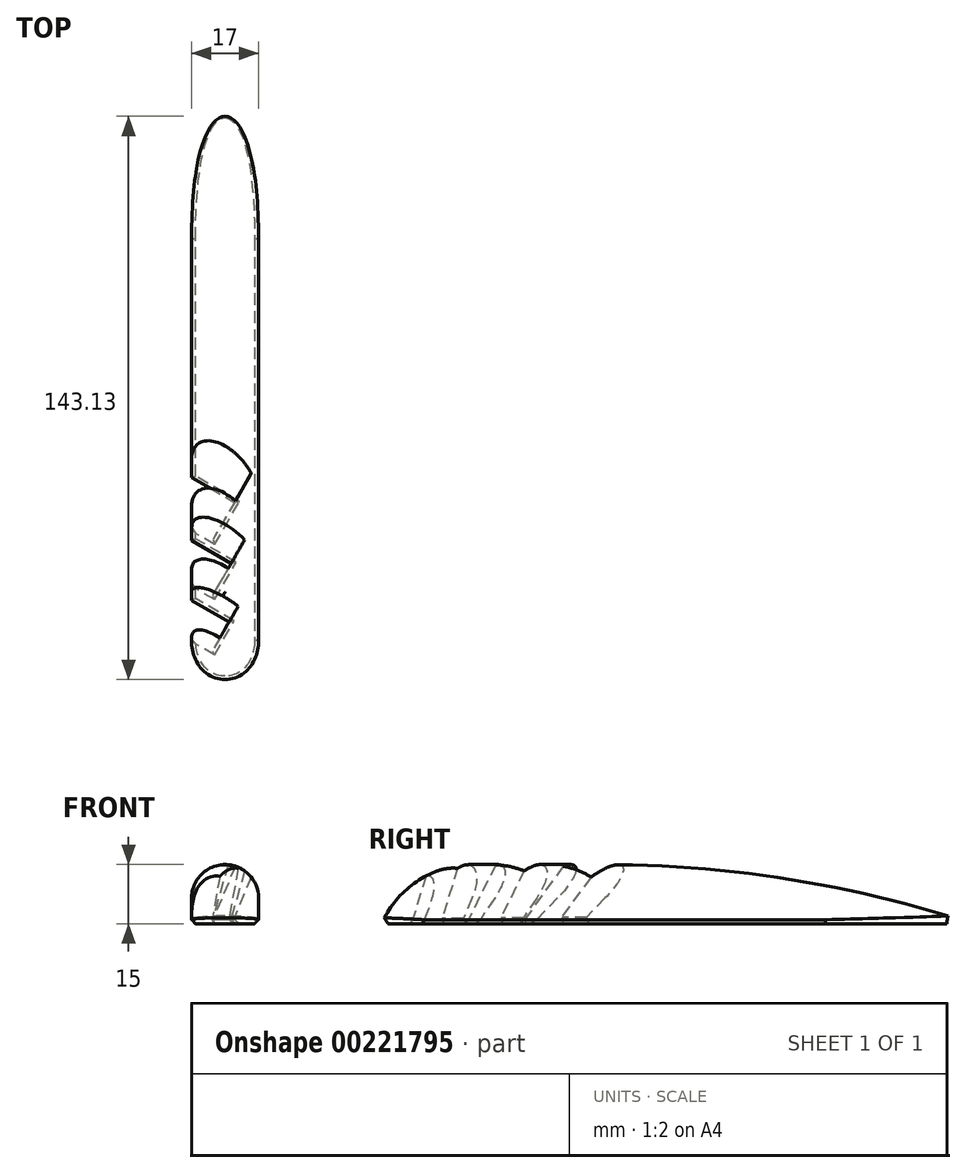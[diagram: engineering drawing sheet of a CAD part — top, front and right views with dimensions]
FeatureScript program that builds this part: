
annotation { "Feature Type Name" : "Feature", "Feature Type Description" : "" }
export const myFeature = defineFeature(function(context is Context, id is Id, definition is map)
    precondition{}
    {
        {
            var Q0;
            Q0=qCreatedBy(makeId("Top.planeOp"),FACE);
            var sketch = newSketch(context, id + "F0", { "sketchPlane" : qUnion([Q0])});
            skLineSegment(sketch, "E0.bottom", {"start": v(8.5, 75) * mm, "end": v(-8.5, 75) * mm});
            skLineSegment(sketch, "E0.top", {"start": v(8.5, -75) * mm, "end": v(-8.5, -75) * mm});
            skLineSegment(sketch, "E0.left", {"start": v(8.5, 75) * mm, "end": v(8.5, -75) * mm});
            skLineSegment(sketch, "E0.right", {"start": v(-8.5, 75) * mm, "end": v(-8.5, -75) * mm});
            skPoint(sketch, "E0.middle", {"position": v(0, 0) * mm});
            skSolve(sketch);
        }
        {
            var Q0;
            Q0=makeQuery(id+"F0.imprint","IMPRINT",FACE,{"disambiguationData":[TD([[makeQuery(id+"F0.imprint","IMPRINT",EDGE,{"derivedFrom":sQuery(id+"F0.wireOp",EDGE,"E0.bottom")}),1.0]])]});
            extrude(context, id + "F1", {"entities" : qUnion([Q0]), "depth" : 15 * mm, "offsetDistance" : 25 * mm});
        }
        {
            var Q0;
            Q0=makeQuery(id+"F1.opExtrude","CAP_FACE",FACE,{"disambiguationData":[OSD([sQuery(id+"F0.wireOp",EDGE,"E0.bottom"),sQuery(id+"F0.wireOp",EDGE,"E0.top"),sQuery(id+"F0.wireOp",EDGE,"E0.left"),sQuery(id+"F0.wireOp",EDGE,"E0.right")])],"isStart":true});
            var sketch = newSketch(context, id + "F2", { "sketchPlane" : qUnion([Q0])});
            skLineSegment(sketch, "E1", {"start": v(-3.5, 75) * mm, "end": v(-3.5, -75) * mm, "construction": true});
            skLineSegment(sketch, "E2", {"start": v(-3.5, 67.5) * mm, "end": v(-8.5, 64.61) * mm});
            skLineSegment(sketch, "E3.0.1.0", {"start": v(-3.5, 53.5) * mm, "end": v(-8.5, 50.61) * mm});
            skLineSegment(sketch, "E3.0.2.0", {"start": v(-3.5, 39.5) * mm, "end": v(-8.5, 36.61) * mm});
            skLineSegment(sketch, "E3.direction1", {"start": v(-8.5, 64.61) * mm, "end": v(-8.5, 64.61) * mm});
            skLineSegment(sketch, "E3.direction2", {"start": v(-8.5, 64.61) * mm, "end": v(-8.5, 50.61) * mm, "construction": true});
            skSolve(sketch);
        }
        {
            var Q0;
            Q0=sQuery(id+"F2.wireOp",EDGE,"E2");
            var Q1;
            {var subQ1=makeQuery(id+"F1.opExtrude","CAP_EDGE",EDGE,{"disambiguationData":[OSD([sQuery(id+"F0.wireOp",EDGE,"E0.bottom")])],"isStart":true});Q1=makeQuery(id+"F2.imprint","IMPRINT",FACE,{"disambiguationData":[TD([[makeQuery(id+"F2.imprint","IMPRINT",EDGE,{"derivedFrom":subQ1}),-1.0]])]});}
            cPlane(context, id + "F3", {"entities" : qUnion([Q0, Q1]), "cplaneType" : CPlaneType.LINE_ANGLE, "offset" : 25 * mm, "angle" : 20 * degree, "width" : 150 * mm, "height" : 150 * mm});
        }
        {
            var Q0;
            Q0=qCreatedBy(id+"F3.planeOp",FACE);
            var sketch = newSketch(context, id + "F4", { "sketchPlane" : qUnion([Q0])});
            skLineSegment(sketch, "E4.0", {"start": v(0.02, -64.38) * mm, "end": v(-5.05, -61.62) * mm});
            skLineSegment(sketch, "E4.1", {"start": v(-14.68, 67.02) * mm, "end": v(-6.97, -76.04) * mm});
            skLineSegment(sketch, "E5", {"start": v(-5.05, -61.62) * mm, "end": v(-7.82, -60.12) * mm});
            skLineSegment(sketch, "E6", {"start": v(0.02, -64.38) * mm, "end": v(3.84, -57.35) * mm});
            skLineSegment(sketch, "E7", {"start": v(3.84, -57.35) * mm, "end": v(-8.33, -50.75) * mm});
            skSolve(sketch);
        }
        {
            var Q0;
            Q0=makeQuery(id+"F4.imprint","IMPRINT",FACE,{"disambiguationData":[TD([[makeQuery(id+"F4.imprint","IMPRINT",EDGE,{"derivedFrom":sQuery(id+"F4.wireOp",EDGE,"E4.0")}),-1.0]])]});
            var Q1;
            Q1=makeQuery(id+"F1.opExtrude","CAP_FACE",FACE,{"disambiguationData":[OSD([sQuery(id+"F0.wireOp",EDGE,"E0.bottom"),sQuery(id+"F0.wireOp",EDGE,"E0.top"),sQuery(id+"F0.wireOp",EDGE,"E0.left"),sQuery(id+"F0.wireOp",EDGE,"E0.right")])],"isStart":false});
            extrude(context, id + "F5", {"entities" : qUnion([Q0]), "operationType" : NewBodyOperationType.REMOVE, "endBound" : BoundingType.UP_TO_SURFACE, "depth" : 25 * mm, "endBoundEntityFace" : qUnion([Q1]), "offsetDistance" : 25 * mm});
        }
        {
            var Q0;
            Q0=sQuery(id+"F2.wireOp",EDGE,"E3.0.1.0");
            var Q1;
            {var subQ1=makeQuery(id+"F1.opExtrude","CAP_EDGE",EDGE,{"disambiguationData":[OSD([sQuery(id+"F0.wireOp",EDGE,"E0.bottom")])],"isStart":true});Q1=makeQuery(id+"F2.imprint","IMPRINT",FACE,{"disambiguationData":[TD([[makeQuery(id+"F2.imprint","IMPRINT",EDGE,{"derivedFrom":subQ1}),-1.0]])]});}
            cPlane(context, id + "F6", {"entities" : qUnion([Q0, Q1]), "cplaneType" : CPlaneType.LINE_ANGLE, "offset" : 25 * mm, "angle" : 30 * degree, "width" : 150 * mm, "height" : 150 * mm});
        }
        {
            var Q0;
            Q0=qCreatedBy(id+"F6.planeOp",FACE);
            var sketch = newSketch(context, id + "F7", { "sketchPlane" : qUnion([Q0])});
            skLineSegment(sketch, "E8.0", {"start": v(2.6, -47.85) * mm, "end": v(-2.57, -45.27) * mm});
            skLineSegment(sketch, "E8.1", {"start": v(-19.97, 60.37) * mm, "end": v(-6.16, -50.07) * mm});
            skLineSegment(sketch, "E9", {"start": v(-2.57, -45.27) * mm, "end": v(-7.04, -43.03) * mm});
            skLineSegment(sketch, "E10", {"start": v(2.6, -47.85) * mm, "end": v(6.17, -40.7) * mm});
            skLineSegment(sketch, "E11", {"start": v(6.17, -40.7) * mm, "end": v(-8.24, -33.5) * mm});
            skSolve(sketch);
        }
        {
            var Q0;
            Q0=makeQuery(id+"F7.imprint","IMPRINT",FACE,{"disambiguationData":[TD([[makeQuery(id+"F7.imprint","IMPRINT",EDGE,{"derivedFrom":sQuery(id+"F7.wireOp",EDGE,"E8.0")}),-1.0]])]});
            var Q1;
            Q1=makeQuery(id+"F1.opExtrude","CAP_FACE",FACE,{"disambiguationData":[OSD([sQuery(id+"F0.wireOp",EDGE,"E0.bottom"),sQuery(id+"F0.wireOp",EDGE,"E0.top"),sQuery(id+"F0.wireOp",EDGE,"E0.left"),sQuery(id+"F0.wireOp",EDGE,"E0.right")])],"isStart":false});
            extrude(context, id + "F8", {"entities" : qUnion([Q0]), "operationType" : NewBodyOperationType.REMOVE, "endBound" : BoundingType.UP_TO_SURFACE, "depth" : 25 * mm, "endBoundEntityFace" : qUnion([Q1]), "offsetDistance" : 25 * mm});
        }
        {
            var Q0;
            Q0=sQuery(id+"F2.wireOp",EDGE,"E3.0.2.0");
            var Q1;
            {var subQ1=makeQuery(id+"F1.opExtrude","CAP_EDGE",EDGE,{"disambiguationData":[OSD([sQuery(id+"F0.wireOp",EDGE,"E0.bottom")])],"isStart":true});Q1=makeQuery(id+"F2.imprint","IMPRINT",FACE,{"disambiguationData":[TD([[makeQuery(id+"F2.imprint","IMPRINT",EDGE,{"derivedFrom":subQ1}),-1.0]])]});}
            cPlane(context, id + "F9", {"entities" : qUnion([Q0, Q1]), "cplaneType" : CPlaneType.LINE_ANGLE, "offset" : 25 * mm, "angle" : 40 * degree, "width" : 150 * mm, "height" : 150 * mm});
        }
        {
            var Q0;
            Q0=qCreatedBy(id+"F9.planeOp",FACE);
            var sketch = newSketch(context, id + "F10", { "sketchPlane" : qUnion([Q0])});
            skLineSegment(sketch, "E12.0", {"start": v(4.15, -31.95) * mm, "end": v(-1.13, -29.62) * mm});
            skLineSegment(sketch, "E12.1", {"start": v(-26.12, 51.85) * mm, "end": v(-6.3, -33.04) * mm});
            skLineSegment(sketch, "E13", {"start": v(-1.13, -29.62) * mm, "end": v(-7.78, -26.68) * mm});
            skLineSegment(sketch, "E14", {"start": v(4.15, -31.95) * mm, "end": v(7.38, -24.64) * mm});
            skLineSegment(sketch, "E15", {"start": v(7.38, -24.64) * mm, "end": v(-10.06, -16.92) * mm});
            skSolve(sketch);
        }
        {
            var Q0;
            Q0=makeQuery(id+"F10.imprint","IMPRINT",FACE,{"disambiguationData":[TD([[makeQuery(id+"F10.imprint","IMPRINT",EDGE,{"derivedFrom":sQuery(id+"F10.wireOp",EDGE,"E12.0")}),-1.0]])]});
            var Q1;
            {var subQ0=sQuery(id+"F0.wireOp",EDGE,"E0.bottom");var subQ1=sQuery(id+"F0.wireOp",EDGE,"E0.right");var subQ2=sQuery(id+"F0.wireOp",EDGE,"E0.left");Q1=makeQuery(id+"F8.boolean.opBoolean","SPLIT",FACE,{"disambiguationData":[TD([makeQuery(id+"F1.opExtrude","SWEPT_FACE",FACE,{"disambiguationData":[OSD([subQ0])]})])],"derivedFrom":makeQuery(id+"F1.opExtrude","CAP_FACE",FACE,{"disambiguationData":[OSD([subQ0,sQuery(id+"F0.wireOp",EDGE,"E0.top"),subQ2,subQ1])],"isStart":false})});}
            extrude(context, id + "F11", {"entities" : qUnion([Q0]), "operationType" : NewBodyOperationType.REMOVE, "endBound" : BoundingType.UP_TO_SURFACE, "depth" : 25 * mm, "endBoundEntityFace" : qUnion([Q1]), "offsetDistance" : 25 * mm});
        }
        {
            var Q0;
            Q0=makeQuery(id+"F1.opExtrude","CAP_EDGE",EDGE,{"disambiguationData":[OSD([sQuery(id+"F0.wireOp",EDGE,"E0.bottom")])],"isStart":false});
            fillet(context, id + "F12", {"entities" : qUnion([Q0]), "radius" : 300 * mm, "tangentPropagation" : true, "allowEdgeOverflow" : false});
        }
        {
            var Q0;
            Q0=makeQuery(id+"F1.opExtrude","CAP_EDGE",EDGE,{"disambiguationData":[OSD([sQuery(id+"F0.wireOp",EDGE,"E0.top")])],"isStart":false});
            fillet(context, id + "F13", {"entities" : qUnion([Q0]), "radius" : 25 * mm, "tangentPropagation" : true, "allowEdgeOverflow" : false});
        }
        {
            var Q0;
            {var subQ0=sQuery(id+"F0.wireOp",EDGE,"E0.bottom");var subQ1=makeQuery(id+"F1.opExtrude","SWEPT_FACE",FACE,{"disambiguationData":[OSD([subQ0])]});var subQ2=sQuery(id+"F0.wireOp",EDGE,"E0.right");Q0=makeQuery(id+"F12.opFillet","BLEND_EDGE",EDGE,{"blendedFrom":[makeQuery(id+"F1.opExtrude","CAP_EDGE",EDGE,{"disambiguationData":[OSD([subQ0])],"isStart":false}),makeQuery(id+"F11.boolean.opBoolean","SPLIT",FACE,{"disambiguationData":[TD([subQ1])],"derivedFrom":makeQuery(id+"F8.boolean.opBoolean","SPLIT",FACE,{"disambiguationData":[TD([subQ1])],"derivedFrom":makeQuery(id+"F5.boolean.opBoolean","SPLIT",FACE,{"disambiguationData":[TD([subQ1])],"derivedFrom":makeQuery(id+"F1.opExtrude","SWEPT_FACE",FACE,{"disambiguationData":[OSD([subQ2])]})})})})],"blendedInto":[makeQuery(id+"F11.boolean.opBoolean","SPLIT",FACE,{"disambiguationData":[TD([subQ1])],"derivedFrom":makeQuery(id+"F8.boolean.opBoolean","SPLIT",FACE,{"disambiguationData":[TD([subQ1])],"derivedFrom":makeQuery(id+"F5.boolean.opBoolean","SPLIT",FACE,{"disambiguationData":[TD([subQ1])],"derivedFrom":makeQuery(id+"F1.opExtrude","SWEPT_FACE",FACE,{"disambiguationData":[OSD([subQ2])]})})})})]});}
            var Q1;
            {var subQ0=sQuery(id+"F0.wireOp",EDGE,"E0.right");var subQ1=sQuery(id+"F0.wireOp",EDGE,"E0.bottom");var subQ4=makeQuery(id+"F8.opExtrude","SWEPT_FACE",FACE,{"disambiguationData":[OSD([sQuery(id+"F7.wireOp",EDGE,"E11")])]});var subQ5=makeQuery(id+"F1.opExtrude","SWEPT_FACE",FACE,{"disambiguationData":[OSD([subQ1])]});Q1=makeQuery(id+"F11.boolean.opBoolean","SPLIT",EDGE,{"disambiguationData":[TD([makeQuery(id+"F8.boolean.opBoolean","COPY",FACE,{"derivedFrom":subQ4})])],"derivedFrom":makeQuery(id+"F8.boolean.opBoolean","SPLIT",EDGE,{"disambiguationData":[TD([subQ5])],"derivedFrom":makeQuery(id+"F5.boolean.opBoolean","SPLIT",EDGE,{"disambiguationData":[TD([subQ5])],"derivedFrom":makeQuery(id+"F1.opExtrude","CAP_EDGE",EDGE,{"disambiguationData":[OSD([subQ0])],"isStart":false})})})});}
            var Q2;
            {var subQ0=sQuery(id+"F0.wireOp",EDGE,"E0.right");var subQ1=sQuery(id+"F0.wireOp",EDGE,"E0.bottom");var subQ4=makeQuery(id+"F5.opExtrude","SWEPT_FACE",FACE,{"disambiguationData":[OSD([sQuery(id+"F4.wireOp",EDGE,"E7")])]});Q2=makeQuery(id+"F8.boolean.opBoolean","SPLIT",EDGE,{"disambiguationData":[TD([makeQuery(id+"F5.boolean.opBoolean","COPY",FACE,{"derivedFrom":subQ4})])],"derivedFrom":makeQuery(id+"F5.boolean.opBoolean","SPLIT",EDGE,{"disambiguationData":[TD([makeQuery(id+"F1.opExtrude","SWEPT_FACE",FACE,{"disambiguationData":[OSD([subQ1])]})])],"derivedFrom":makeQuery(id+"F1.opExtrude","CAP_EDGE",EDGE,{"disambiguationData":[OSD([subQ0])],"isStart":false})})});}
            var Q3;
            {var subQ0=sQuery(id+"F0.wireOp",EDGE,"E0.right");var subQ2=sQuery(id+"F0.wireOp",EDGE,"E0.top");Q3=makeQuery(id+"F13.opFillet","BLEND_EDGE",EDGE,{"blendedFrom":[makeQuery(id+"F1.opExtrude","CAP_EDGE",EDGE,{"disambiguationData":[OSD([subQ2])],"isStart":false}),makeQuery(id+"F5.boolean.opBoolean","SPLIT",FACE,{"disambiguationData":[TD([makeQuery(id+"F1.opExtrude","SWEPT_FACE",FACE,{"disambiguationData":[OSD([subQ2])]})])],"derivedFrom":makeQuery(id+"F1.opExtrude","SWEPT_FACE",FACE,{"disambiguationData":[OSD([subQ0])]})})],"blendedInto":[makeQuery(id+"F5.boolean.opBoolean","SPLIT",FACE,{"disambiguationData":[TD([makeQuery(id+"F1.opExtrude","SWEPT_FACE",FACE,{"disambiguationData":[OSD([subQ2])]})])],"derivedFrom":makeQuery(id+"F1.opExtrude","SWEPT_FACE",FACE,{"disambiguationData":[OSD([subQ0])]})})]});}
            var Q4;
            Q4=makeQuery(id+"F12.opFillet","BLEND_EDGE",EDGE,{"blendedFrom":[makeQuery(id+"F1.opExtrude","CAP_EDGE",EDGE,{"disambiguationData":[OSD([sQuery(id+"F0.wireOp",EDGE,"E0.bottom")])],"isStart":false}),makeQuery(id+"F1.opExtrude","SWEPT_FACE",FACE,{"disambiguationData":[OSD([sQuery(id+"F0.wireOp",EDGE,"E0.left")])]})],"blendedInto":[makeQuery(id+"F1.opExtrude","SWEPT_FACE",FACE,{"disambiguationData":[OSD([sQuery(id+"F0.wireOp",EDGE,"E0.left")])]})]});
            fillet(context, id + "F14", {"entities" : qUnion([Q0, Q1, Q2, Q3, Q4]), "radius" : 8.5 * mm, "tangentPropagation" : true, "allowEdgeOverflow" : false});
        }
        {
            var Q0;
            Q0=makeQuery(id+"F1.opExtrude","CAP_EDGE",EDGE,{"disambiguationData":[OSD([sQuery(id+"F0.wireOp",EDGE,"E0.left")])],"isStart":true});
            var Q1;
            {var subQ0=sQuery(id+"F0.wireOp",EDGE,"E0.right");var subQ1=sQuery(id+"F0.wireOp",EDGE,"E0.bottom");var subQ4=makeQuery(id+"F8.opExtrude","SWEPT_FACE",FACE,{"disambiguationData":[OSD([sQuery(id+"F7.wireOp",EDGE,"E11")])]});var subQ5=makeQuery(id+"F1.opExtrude","SWEPT_FACE",FACE,{"disambiguationData":[OSD([subQ1])]});Q1=makeQuery(id+"F11.boolean.opBoolean","SPLIT",EDGE,{"disambiguationData":[TD([makeQuery(id+"F8.boolean.opBoolean","COPY",FACE,{"derivedFrom":subQ4})])],"derivedFrom":makeQuery(id+"F8.boolean.opBoolean","SPLIT",EDGE,{"disambiguationData":[TD([subQ5])],"derivedFrom":makeQuery(id+"F5.boolean.opBoolean","SPLIT",EDGE,{"disambiguationData":[TD([subQ5])],"derivedFrom":makeQuery(id+"F1.opExtrude","CAP_EDGE",EDGE,{"disambiguationData":[OSD([subQ0])],"isStart":true})})})});}
            var Q2;
            {var subQ0=sQuery(id+"F0.wireOp",EDGE,"E0.right");var subQ1=sQuery(id+"F0.wireOp",EDGE,"E0.bottom");var subQ4=makeQuery(id+"F5.opExtrude","SWEPT_FACE",FACE,{"disambiguationData":[OSD([sQuery(id+"F4.wireOp",EDGE,"E7")])]});Q2=makeQuery(id+"F8.boolean.opBoolean","SPLIT",EDGE,{"disambiguationData":[TD([makeQuery(id+"F5.boolean.opBoolean","COPY",FACE,{"derivedFrom":subQ4})])],"derivedFrom":makeQuery(id+"F5.boolean.opBoolean","SPLIT",EDGE,{"disambiguationData":[TD([makeQuery(id+"F1.opExtrude","SWEPT_FACE",FACE,{"disambiguationData":[OSD([subQ1])]})])],"derivedFrom":makeQuery(id+"F1.opExtrude","CAP_EDGE",EDGE,{"disambiguationData":[OSD([subQ0])],"isStart":true})})});}
            chamfer(context, id + "F15", {"entities" : qUnion([Q0, Q1, Q2]), "width" : 1 * mm, "tangentPropagation" : true});
        }
        {
            var Q0;
            Q0=makeQuery(id+"F11.boolean.opBoolean","INTERSECT",EDGE,{"derivedFrom":[makeQuery(id+"F1.opExtrude","CAP_FACE",FACE,{"disambiguationData":[OSD([sQuery(id+"F0.wireOp",EDGE,"E0.bottom"),sQuery(id+"F0.wireOp",EDGE,"E0.top"),sQuery(id+"F0.wireOp",EDGE,"E0.left"),sQuery(id+"F0.wireOp",EDGE,"E0.right")])],"isStart":true}),makeQuery(id+"F11.opExtrude","SWEPT_FACE",FACE,{"disambiguationData":[OSD([sQuery(id+"F10.wireOp",EDGE,"E15")])]})]});
            var Q1;
            Q1=makeQuery(id+"F11.boolean.opBoolean","INTERSECT",EDGE,{"derivedFrom":[makeQuery(id+"F1.opExtrude","CAP_FACE",FACE,{"disambiguationData":[OSD([sQuery(id+"F0.wireOp",EDGE,"E0.bottom"),sQuery(id+"F0.wireOp",EDGE,"E0.top"),sQuery(id+"F0.wireOp",EDGE,"E0.left"),sQuery(id+"F0.wireOp",EDGE,"E0.right")])],"isStart":true}),makeQuery(id+"F11.opExtrude","SWEPT_FACE",FACE,{"disambiguationData":[OSD([sQuery(id+"F10.wireOp",EDGE,"E14")])]})]});
            var Q2;
            Q2=makeQuery(id+"F11.boolean.opBoolean","COPY",EDGE,{"derivedFrom":makeQuery(id+"F11.opExtrude","CAP_EDGE",EDGE,{"disambiguationData":[OSD([sQuery(id+"F10.wireOp",EDGE,"E12.0"),sQuery(id+"F10.wireOp",EDGE,"E13")])],"isStart":true})});
            var Q3;
            Q3=makeQuery(id+"F8.boolean.opBoolean","INTERSECT",EDGE,{"derivedFrom":[makeQuery(id+"F1.opExtrude","CAP_FACE",FACE,{"disambiguationData":[OSD([sQuery(id+"F0.wireOp",EDGE,"E0.bottom"),sQuery(id+"F0.wireOp",EDGE,"E0.top"),sQuery(id+"F0.wireOp",EDGE,"E0.left"),sQuery(id+"F0.wireOp",EDGE,"E0.right")])],"isStart":true}),makeQuery(id+"F8.opExtrude","SWEPT_FACE",FACE,{"disambiguationData":[OSD([sQuery(id+"F7.wireOp",EDGE,"E11")])]})]});
            var Q4;
            Q4=makeQuery(id+"F8.boolean.opBoolean","INTERSECT",EDGE,{"derivedFrom":[makeQuery(id+"F1.opExtrude","CAP_FACE",FACE,{"disambiguationData":[OSD([sQuery(id+"F0.wireOp",EDGE,"E0.bottom"),sQuery(id+"F0.wireOp",EDGE,"E0.top"),sQuery(id+"F0.wireOp",EDGE,"E0.left"),sQuery(id+"F0.wireOp",EDGE,"E0.right")])],"isStart":true}),makeQuery(id+"F8.opExtrude","SWEPT_FACE",FACE,{"disambiguationData":[OSD([sQuery(id+"F7.wireOp",EDGE,"E10")])]})]});
            var Q5;
            Q5=makeQuery(id+"F8.boolean.opBoolean","COPY",EDGE,{"derivedFrom":makeQuery(id+"F8.opExtrude","CAP_EDGE",EDGE,{"disambiguationData":[OSD([sQuery(id+"F7.wireOp",EDGE,"E8.0"),sQuery(id+"F7.wireOp",EDGE,"E9")])],"isStart":true})});
            var Q6;
            Q6=makeQuery(id+"F5.boolean.opBoolean","INTERSECT",EDGE,{"derivedFrom":[makeQuery(id+"F1.opExtrude","CAP_FACE",FACE,{"disambiguationData":[OSD([sQuery(id+"F0.wireOp",EDGE,"E0.bottom"),sQuery(id+"F0.wireOp",EDGE,"E0.top"),sQuery(id+"F0.wireOp",EDGE,"E0.left"),sQuery(id+"F0.wireOp",EDGE,"E0.right")])],"isStart":true}),makeQuery(id+"F5.opExtrude","SWEPT_FACE",FACE,{"disambiguationData":[OSD([sQuery(id+"F4.wireOp",EDGE,"E7")])]})]});
            var Q7;
            Q7=makeQuery(id+"F5.boolean.opBoolean","INTERSECT",EDGE,{"derivedFrom":[makeQuery(id+"F1.opExtrude","CAP_FACE",FACE,{"disambiguationData":[OSD([sQuery(id+"F0.wireOp",EDGE,"E0.bottom"),sQuery(id+"F0.wireOp",EDGE,"E0.top"),sQuery(id+"F0.wireOp",EDGE,"E0.left"),sQuery(id+"F0.wireOp",EDGE,"E0.right")])],"isStart":true}),makeQuery(id+"F5.opExtrude","SWEPT_FACE",FACE,{"disambiguationData":[OSD([sQuery(id+"F4.wireOp",EDGE,"E6")])]})]});
            var Q8;
            Q8=makeQuery(id+"F5.boolean.opBoolean","COPY",EDGE,{"derivedFrom":makeQuery(id+"F5.opExtrude","CAP_EDGE",EDGE,{"disambiguationData":[OSD([sQuery(id+"F4.wireOp",EDGE,"E4.0"),sQuery(id+"F4.wireOp",EDGE,"E5")])],"isStart":true})});
            chamfer(context, id + "F16", {"entities" : qUnion([Q0, Q1, Q2, Q3, Q4, Q5, Q6, Q7, Q8]), "width" : 1 * mm, "tangentPropagation" : true});
        }
    });
